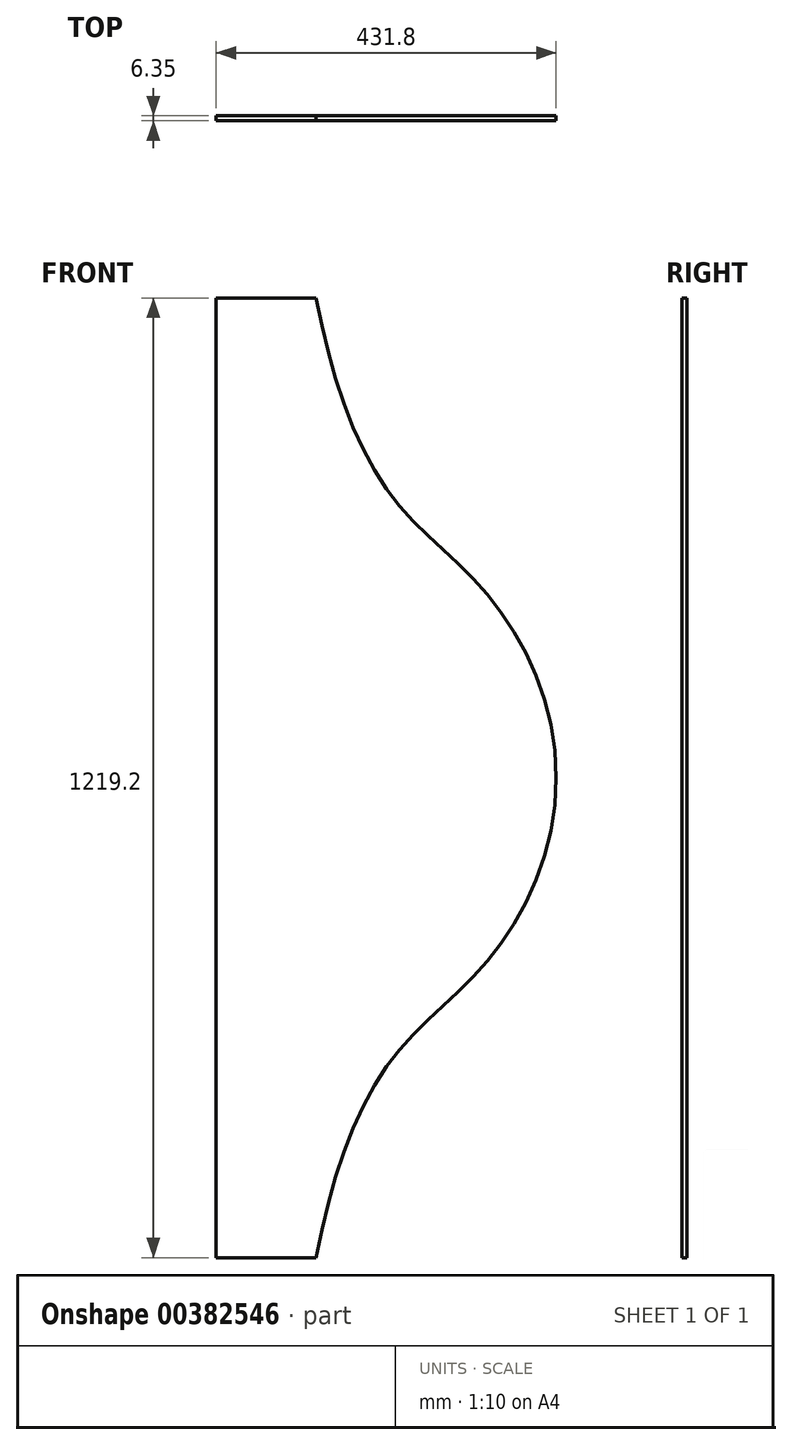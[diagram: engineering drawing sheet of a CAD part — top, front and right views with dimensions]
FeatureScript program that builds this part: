
annotation { "Feature Type Name" : "Feature", "Feature Type Description" : "" }
export const myFeature = defineFeature(function(context is Context, id is Id, definition is map)
    precondition{}
    {
        {
            var Q0;
            Q0=qCreatedBy(makeId("Front.planeOp"),FACE);
            var sketch = newSketch(context, id + "F0", { "sketchPlane" : qUnion([Q0])});
            skLineSegment(sketch, "E0.bottom", {"start": v(304.8, 609.6) * mm, "end": v(-304.8, 609.6) * mm});
            skLineSegment(sketch, "E0.top", {"start": v(304.8, -609.6) * mm, "end": v(-304.8, -609.6) * mm});
            skLineSegment(sketch, "E0.left", {"start": v(304.8, 609.6) * mm, "end": v(304.8, -609.6) * mm});
            skLineSegment(sketch, "E0.right", {"start": v(-304.8, 609.6) * mm, "end": v(-304.8, -609.6) * mm});
            skPoint(sketch, "E0.middle", {"position": v(0, 0) * mm});
            skSolve(sketch);
        }
        {
            var Q0;
            Q0=makeQuery(id+"F0.imprint","IMPRINT",FACE,{"disambiguationData":[TD([[makeQuery(id+"F0.imprint","IMPRINT",EDGE,{"derivedFrom":sQuery(id+"F0.wireOp",EDGE,"E0.bottom")}),1.0]])]});
            extrude(context, id + "F1", {"entities" : qUnion([Q0]), "depth" : 6.35 * mm});
        }
        {
            var Q0;
            Q0=makeQuery(id+"F1.opExtrude","CAP_FACE",FACE,{"disambiguationData":[OSD([sQuery(id+"F0.wireOp",EDGE,"E0.bottom"),sQuery(id+"F0.wireOp",EDGE,"E0.top"),sQuery(id+"F0.wireOp",EDGE,"E0.left"),sQuery(id+"F0.wireOp",EDGE,"E0.right")])],"isStart":false});
            var sketch = newSketch(context, id + "F2", { "sketchPlane" : qUnion([Q0])});
            skFitSpline(sketch, "E1", {"points": [v(304.8, 0) * mm, v(217.87, 232.14) * mm, v(93.25, 361.37) * mm, v(0, 609.6) * mm], "startDerivative": vector(0, 804.41) * mm, "endDerivative": vector(-152.63, 822.12) * mm});
            skFitSpline(sketch, "E2.MirrorCS", {"points": [v(304.8, 0) * mm, v(217.87, -232.14) * mm, v(93.25, -361.37) * mm, v(0, -609.6) * mm], "startDerivative": vector(0, -804.41) * mm, "endDerivative": vector(-152.63, -822.12) * mm});
            skLineSegment(sketch, "E3", {"start": v(0, 609.6) * mm, "end": v(304.8, 609.6) * mm});
            skLineSegment(sketch, "E4", {"start": v(304.8, 609.6) * mm, "end": v(304.8, -609.6) * mm});
            skLineSegment(sketch, "E5", {"start": v(304.8, -609.6) * mm, "end": v(0, -609.6) * mm});
            skLineSegment(sketch, "E6", {"start": v(-127, 609.6) * mm, "end": v(-127, -609.6) * mm});
            skLineSegment(sketch, "E7", {"start": v(-127, 609.6) * mm, "end": v(-304.8, 609.6) * mm});
            skLineSegment(sketch, "E8", {"start": v(-304.8, 609.6) * mm, "end": v(-304.8, -609.6) * mm});
            skLineSegment(sketch, "E9", {"start": v(-304.8, -609.6) * mm, "end": v(-127, -609.6) * mm});
            skSolve(sketch);
        }
        {
            var Q0;
            {var subQ0=sQuery(id+"F2.wireOp",EDGE,"E1");Q0=makeQuery(id+"F2.imprint","IMPRINT",FACE,{"disambiguationData":[TD([[makeQuery(id+"F2.imprint","IMPRINT",EDGE,{"derivedFrom":subQ0}),-1.0]])]});}
            var Q1;
            {var subQ0=sQuery(id+"F2.wireOp",EDGE,"E2.MirrorCS");Q1=makeQuery(id+"F2.imprint","IMPRINT",FACE,{"disambiguationData":[TD([[makeQuery(id+"F2.imprint","IMPRINT",EDGE,{"derivedFrom":subQ0}),1.0]])]});}
            var Q2;
            Q2=makeQuery(id+"F2.imprint","IMPRINT",FACE,{"disambiguationData":[TD([[makeQuery(id+"F2.imprint","IMPRINT",EDGE,{"derivedFrom":sQuery(id+"F2.wireOp",EDGE,"E6")}),-1.0]])]});
            extrude(context, id + "F3", {"entities" : qUnion([Q0, Q1, Q2]), "operationType" : NewBodyOperationType.REMOVE, "endBound" : BoundingType.THROUGH_ALL, "oppositeDirection" : true, "depth" : 25.4 * mm});
        }
    });
